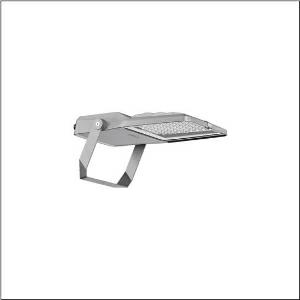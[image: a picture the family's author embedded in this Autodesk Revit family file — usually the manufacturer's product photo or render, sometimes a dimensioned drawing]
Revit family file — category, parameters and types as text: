
# Revit family: floodlight_fl_21_iq_mini___pl33t_5xa7771b4f1a_48a0
name_source: partatom
category: Lighting Fixtures
units: mm (PartAtom-declared; Revit-internal decimal feet)

## family parameters
Cut with Voids When Loaded = No
Host = Face
Light Source = No
Part Type = Normal
Room Calculation Point = No
Round Connector Dimension = Use Diameter
Shared = No

## types (1)
- --- (1 x LED, 6420 lm, 45.5 W, 4000K)
    Apparent Load = 46 VA
    CIE Flux Codes = 26 75 99 100 100
    Color Rendering = 70
    Color Temperature = 4000K
    Default Elevation = 1800 mm
    Description = Floodlight FL 21 iQ mini, floodlight, primary light control with lens, of PMMA, primary optical cover: protective disc, of toughened safety glass, transparent, light distribution: PL33T, light emission: direct distribution, installation type: surface-mounted, LED, High Power LED, rated luminous flux: 6.420lm, luminous efficacy: 141lm/W, light colour: 740, colour temperature: 4000K, control gear: iQ Comfort/DALI, control: Auto-Match, Temp-Guard, Lumen-Switch, Night-Set, Smart-Wire, Light-Fading, Desk-Remote (wireless, voltage-free reading and setting of iQ features in the workshop via application-optimized NFC function/RFID function), optimised constant luminous flux control (CLO 2.0), with terminal, 6-pole, mains connection: 220..240V, AC, 50/60Hz, start of lifetime: 46W, end of service life: 48W, reduction: 22W, luminaire housing, of diecast aluminium, powder-coated, Siteco® metallic grey (DB 702S), corrosivity category C5 mid according to DIN EN ISO 12944, suitable for swimming pools, chlorine-resistant, sealing non-destructively replaceable, mounting bracket, of steel, galvanised, powder-coated, Siteco® metallic grey (DB 702S), protection rating (complete): IP66, insulation class (complete): insulation class II (safety insulation), certification: CE, ENEC, VDE, protection symbol: D, impact resistance: IK08, permissible operating ambient temperature: -40..+40°C, permissible operating ambient temperature for outdoor applications: -40..+50°C, standard: DIN EN 12944, LABS conformity tested according to VDMA 24364:2018-05, packaging unit: 1 piece

Light Distribution: PL33T
    Height = 70 mm
    Lamp = 1 x LED
    Lamp Light Flux = 6420 lm
    Lamp Power = 45.5 W
    Lamp count = 1
    Length = 485 mm
    Luminous efficacy = 141 lm/W
    Manufacturer = Siteco
    ModVariant = No
    Model = 5XA7771B4F1A
    Mounting Place = Wall
    Mounting Type = Surface mounted
    Number of Poles = 1
    OnlyDefault = Yes
    Power Factor = 1
    Product Name = Floodlight FL 21 iQ mini | PL33T
    Product group = floodlight | wall mounted
    ProductGroupID = 2001
    Protection Class = Protection class II
    Protection Degree = IP 66
    RLX_Detail_Level = 1
    RLX_Emergency_Light_Flux = 0 lm
    RLX_Emergency_Type = 0
    RLX_Emergency_Type_DB = No
    RlxData = <blob elided: 96089 chars, md5=199b6042>
    Socket = socket
    Standby Power = 0 W
    System Light Flux = 6420 lm
    System Power = 46 W
    Type Comments = factory setting: luminous flux: 100 % | dim-lin: 254 | 463 mA
    Type Image = l_1006845.jpg
    URL = http://relux.com
    VarID = @adj_150248
    Voltage = 0 V
    Weight = 0.00 kg
    Width = 337 mm

## geometry (parser evidence)
native form markers: Blend x4, Sweep x14
no freeform markers — native parametric forms only
